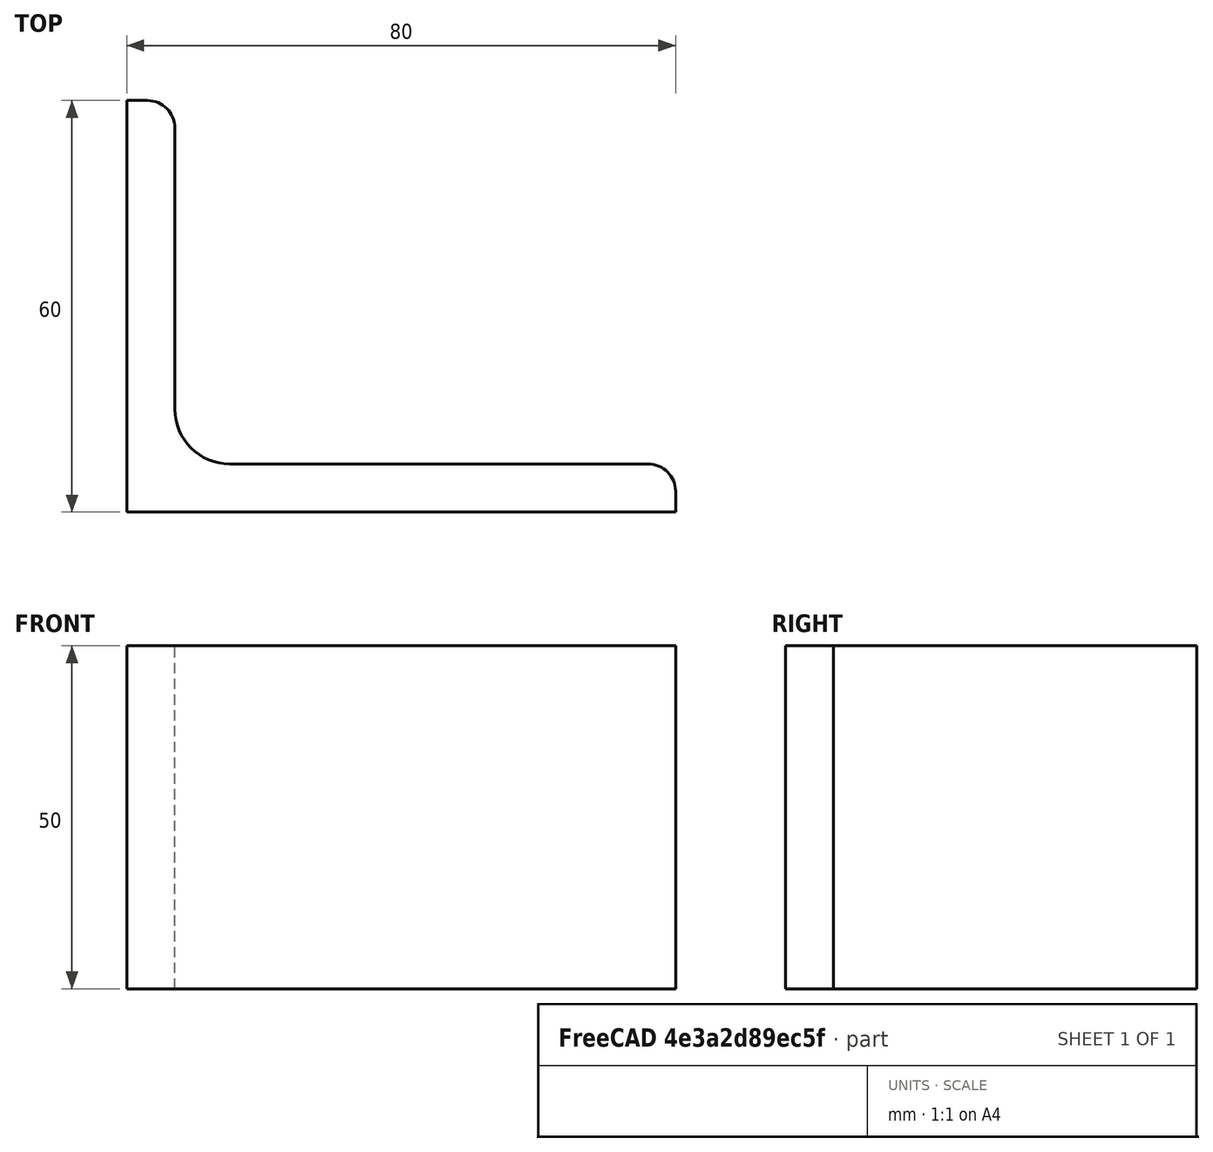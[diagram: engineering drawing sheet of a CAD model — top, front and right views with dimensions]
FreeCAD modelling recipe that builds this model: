
FCSTD DOCUMENT  (FreeCAD 0.15R4671 (Git))
Label: Angle Bar 80x60x7 EN10056 S235JR
License: All rights reserved
LicenseURL: http://en.wikipedia.org/wiki/All_rights_reserved
objects: Sketcher::SketchObject×1, Part::Extrusion×1
note: 2 computed .brp shape members not serialized (recipe doc carries the construction recipe); baked Part::Feature solids carry a one-line shape summary decoded from their .brp

FEATURE [Sketcher::SketchObject] Sketch
  sketch-geometry (9):
    g0: LineSegment StartX=0 StartY=0 StartZ=0 EndX=80 EndY=0 EndZ=0
    g1: LineSegment StartX=80 StartY=0 StartZ=0 EndX=80 EndY=3 EndZ=0
    g2: LineSegment StartX=76 StartY=7 StartZ=0 EndX=15 EndY=7 EndZ=0
    g3: LineSegment StartX=0 StartY=0 StartZ=0 EndX=0 EndY=60 EndZ=0
    g4: LineSegment StartX=0 StartY=60 StartZ=0 EndX=3 EndY=60 EndZ=0
    g5: LineSegment StartX=7 StartY=56 StartZ=0 EndX=7 EndY=15 EndZ=0
    g6: ArcOfCircle CenterX=15 CenterY=15 CenterZ=0 NormalX=0 NormalY=0 NormalZ=1 Radius=8 StartAngle=3.14159 EndAngle=4.71239
    g7: ArcOfCircle CenterX=3 CenterY=56 CenterZ=0 NormalX=0 NormalY=0 NormalZ=1 Radius=4 StartAngle=0 EndAngle=1.5708
    g8: ArcOfCircle CenterX=76 CenterY=3 CenterZ=0 NormalX=0 NormalY=0 NormalZ=1 Radius=4 StartAngle=0 EndAngle=1.5708
  constraints (23):
    c: Coincident(g0,g-1)
    c: Horizontal(g0)
    c: Coincident(g1,g0)
    c: Vertical(g1)
    c: Horizontal(g2)
    c: Coincident(g3,g-1)
    c: Vertical(g3)
    c: Coincident(g4,g3)
    c: Horizontal(g4)
    c: Vertical(g5)
    c: Tangent(g5,g6) = -1.5708
    c: Tangent(g2,g6) = 1.5708
    c: Tangent(g4,g7) = 1.5708
    c: Tangent(g5,g7) = 1.5708
    c: Tangent(g2,g8) = -1.5708
    c: Tangent(g1,g8) = -1.5708
    c: DistanceX(g0) = 80
    c: DistanceY(g3) = 60
    c: DistanceY(g0,g2) = 7
    c: DistanceX(g3,g5) = 7
    c: Radius(g6) = 8
    c: Radius(g8) = 4
    c: Radius(g7) = 4
FEATURE [Part::Extrusion] Extrude  label="Angle Bar 80x60x7 EN10056 S235JR"
  Base = -> Sketch
  Dir = (0,0,50)
  Solid = true
